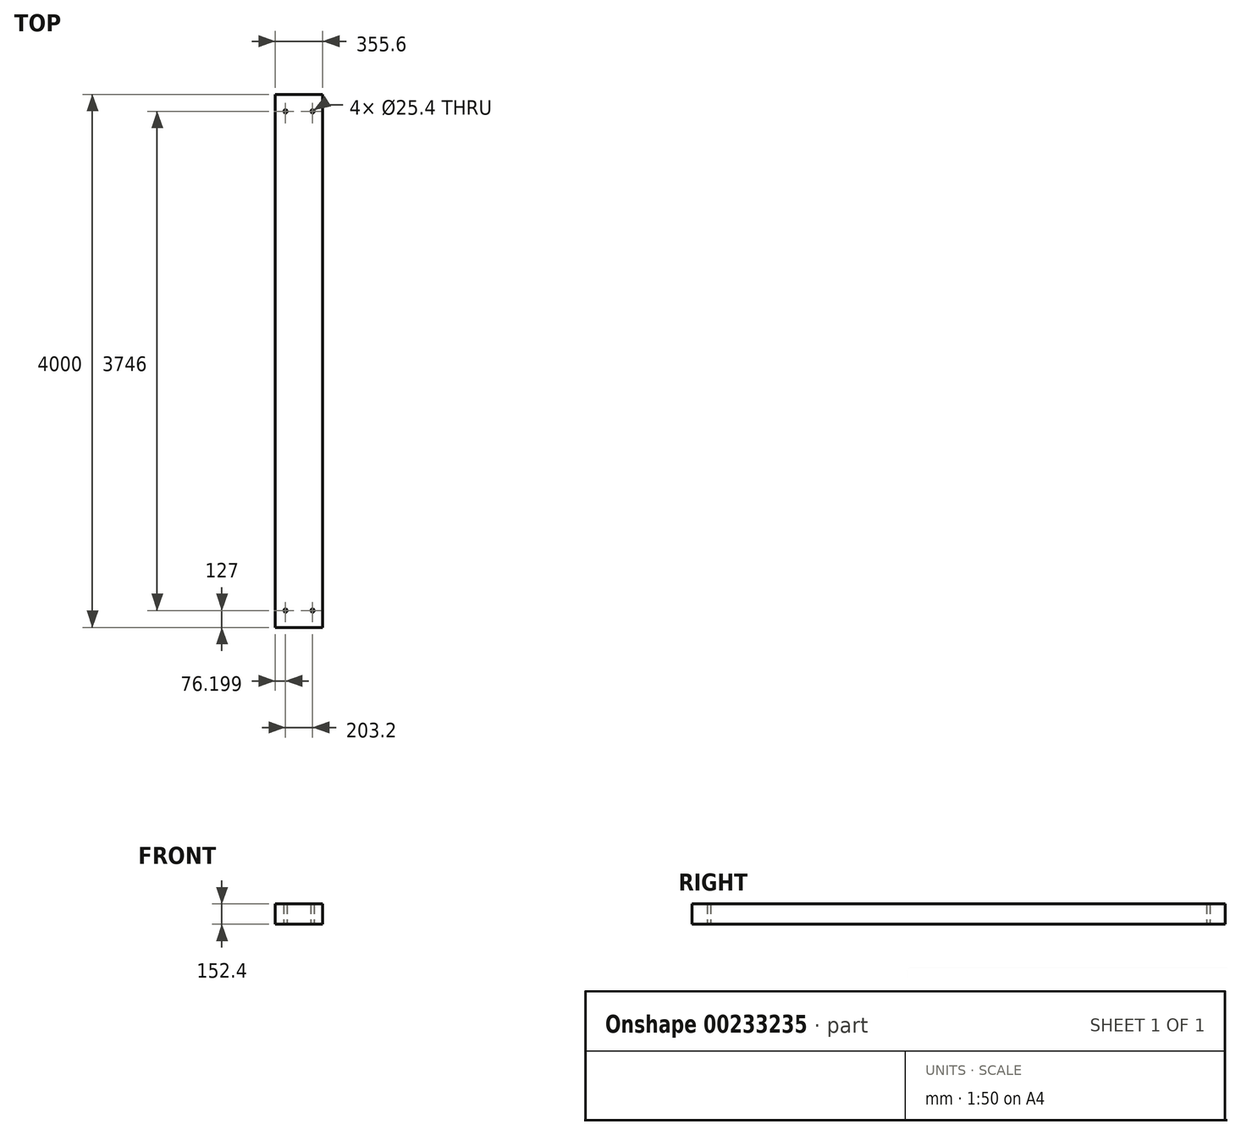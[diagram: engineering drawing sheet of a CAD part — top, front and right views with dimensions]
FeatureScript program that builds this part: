
annotation { "Feature Type Name" : "Feature", "Feature Type Description" : "" }
export const myFeature = defineFeature(function(context is Context, id is Id, definition is map)
    precondition{}
    {
        {
            var Q0;
            Q0=qCreatedBy(makeId("Top.planeOp"),FACE);
            var sketch = newSketch(context, id + "F0", { "sketchPlane" : qUnion([Q0])});
            skLineSegment(sketch, "E0.bottom", {"start": v(-1159.88, 1982.53) * mm, "end": v(-804.28, 1982.53) * mm});
            skLineSegment(sketch, "E0.top", {"start": v(-1159.88, -2017.47) * mm, "end": v(-804.28, -2017.47) * mm});
            skLineSegment(sketch, "E0.left", {"start": v(-1159.88, 1982.53) * mm, "end": v(-1159.88, -2017.47) * mm});
            skLineSegment(sketch, "E0.right", {"start": v(-804.28, 1982.53) * mm, "end": v(-804.28, -2017.47) * mm});
            skCircle(sketch, "E1", {"center": v(-1083.68, 1855.53) * mm, "radius": 12.7 * mm});
            skCircle(sketch, "E2", {"center": v(-880.48, 1855.53) * mm, "radius": 12.7 * mm});
            skCircle(sketch, "E3", {"center": v(-1083.68, -1890.47) * mm, "radius": 12.7 * mm});
            skCircle(sketch, "E4", {"center": v(-880.48, -1890.47) * mm, "radius": 12.7 * mm});
            skSolve(sketch);
        }
        {
            var Q0;
            Q0 = qSketchRegion(id + "F0", true);
            extrude(context, id + "F1", {"entities" : qUnion([Q0]), "depth" : 152.4 * mm});
        }
    });
